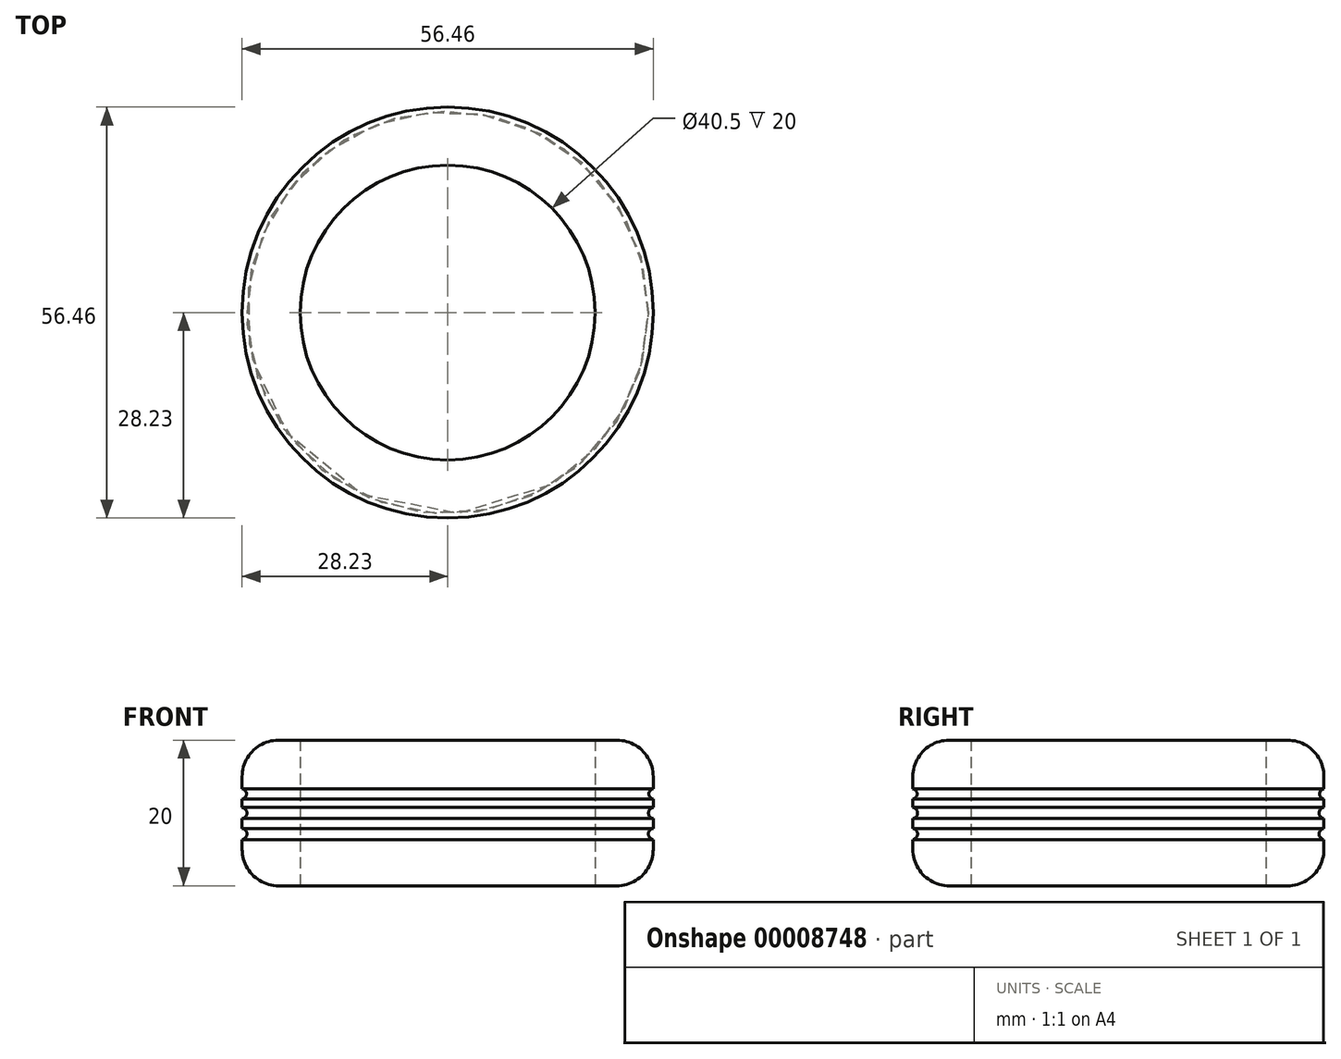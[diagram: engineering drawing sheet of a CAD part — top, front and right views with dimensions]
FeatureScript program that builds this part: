
annotation { "Feature Type Name" : "Feature", "Feature Type Description" : "" }
export const myFeature = defineFeature(function(context is Context, id is Id, definition is map)
    precondition{}
    {
        {
            var Q0;
            Q0=qCreatedBy(makeId("Top.planeOp"),FACE);
            var sketch = newSketch(context, id + "F0", { "sketchPlane" : qUnion([Q0])});
            skCircle(sketch, "E0", {"center": v(0, 0) * mm, "radius": 20.25 * mm});
            skCircle(sketch, "E1", {"center": v(0, 0) * mm, "radius": 28.23 * mm});
            skSolve(sketch);
        }
        {
            var Q0;
            Q0=makeQuery(id+"F0.imprint","IMPRINT",FACE,{"disambiguationData":[TD([[makeQuery(id+"F0.imprint","IMPRINT",EDGE,{"derivedFrom":sQuery(id+"F0.wireOp",EDGE,"E0")}),-1.0]])]});
            extrude(context, id + "F1", {"entities" : qUnion([Q0]), "depth" : 20 * mm});
        }
        {
            var Q0;
            Q0=makeQuery(id+"F1.opExtrude","CAP_EDGE",EDGE,{"disambiguationData":[OSD([sQuery(id+"F0.wireOp",EDGE,"E1")])],"isStart":false});
            var Q1;
            Q1=makeQuery(id+"F1.opExtrude","CAP_EDGE",EDGE,{"disambiguationData":[OSD([sQuery(id+"F0.wireOp",EDGE,"E1")])],"isStart":true});
            fillet(context, id + "F2", {"entities" : qUnion([Q0, Q1]), "radius" : 5 * mm, "tangentPropagation" : true, "allowEdgeOverflow" : false});
        }
        {
            var Q0;
            Q0=qCreatedBy(makeId("Right.planeOp"),FACE);
            var sketch = newSketch(context, id + "F3", { "sketchPlane" : qUnion([Q0])});
            skLineSegment(sketch, "E2", {"start": v(0, 0) * mm, "end": v(0, 27.99) * mm});
            skLineSegment(sketch, "E3", {"start": v(28.35, 6.34) * mm, "end": v(28.35, 7.9) * mm});
            skArc(sketch, "E4", {"start": v(28.35, 10.76) * mm, "mid": v(27.58, 10) * mm, "end": v(28.35, 9.22) * mm});
            skArc(sketch, "E5", {"start": v(28.35, 13.34) * mm, "mid": v(27.63, 12.63) * mm, "end": v(28.35, 11.92) * mm});
            skArc(sketch, "E6", {"start": v(28.35, 7.9) * mm, "mid": v(27.57, 7.12) * mm, "end": v(28.35, 6.34) * mm});
            skPoint(sketch, "E7.orphan", {"position": v(28.35, 15) * mm});
            skLineSegment(sketch, "E8.trimOffspring", {"start": v(28.35, 11.92) * mm, "end": v(28.35, 13.34) * mm});
            skLineSegment(sketch, "E9.trimOffspring", {"start": v(28.35, 9.22) * mm, "end": v(28.35, 10.76) * mm});
            skPoint(sketch, "E10.orphan", {"position": v(28.35, 4.98) * mm});
            skSolve(sketch);
        }
        {
            var Q0;
            Q0=makeQuery(id+"F3.imprint","IMPRINT",FACE,{"disambiguationData":[TD([[makeQuery(id+"F3.imprint","IMPRINT",EDGE,{"derivedFrom":sQuery(id+"F3.wireOp",EDGE,"E5")}),1.0]])]});
            var Q1;
            Q1=makeQuery(id+"F3.imprint","IMPRINT",FACE,{"disambiguationData":[TD([[makeQuery(id+"F3.imprint","IMPRINT",EDGE,{"derivedFrom":sQuery(id+"F3.wireOp",EDGE,"E4")}),1.0]])]});
            var Q2;
            Q2=makeQuery(id+"F3.imprint","IMPRINT",FACE,{"disambiguationData":[TD([[makeQuery(id+"F3.imprint","IMPRINT",EDGE,{"derivedFrom":sQuery(id+"F3.wireOp",EDGE,"E3")}),1.0]])]});
            var Q3;
            Q3=sQuery(id+"F3.wireOp",EDGE,"E2");
            revolve(context, id + "F4", {"operationType" : NewBodyOperationType.REMOVE, "entities" : qUnion([Q0, Q1, Q2]), "axis" : qUnion([Q3]), "revolveType" : RevolveType.FULL, "oppositeDirection" : true});
        }
    });
